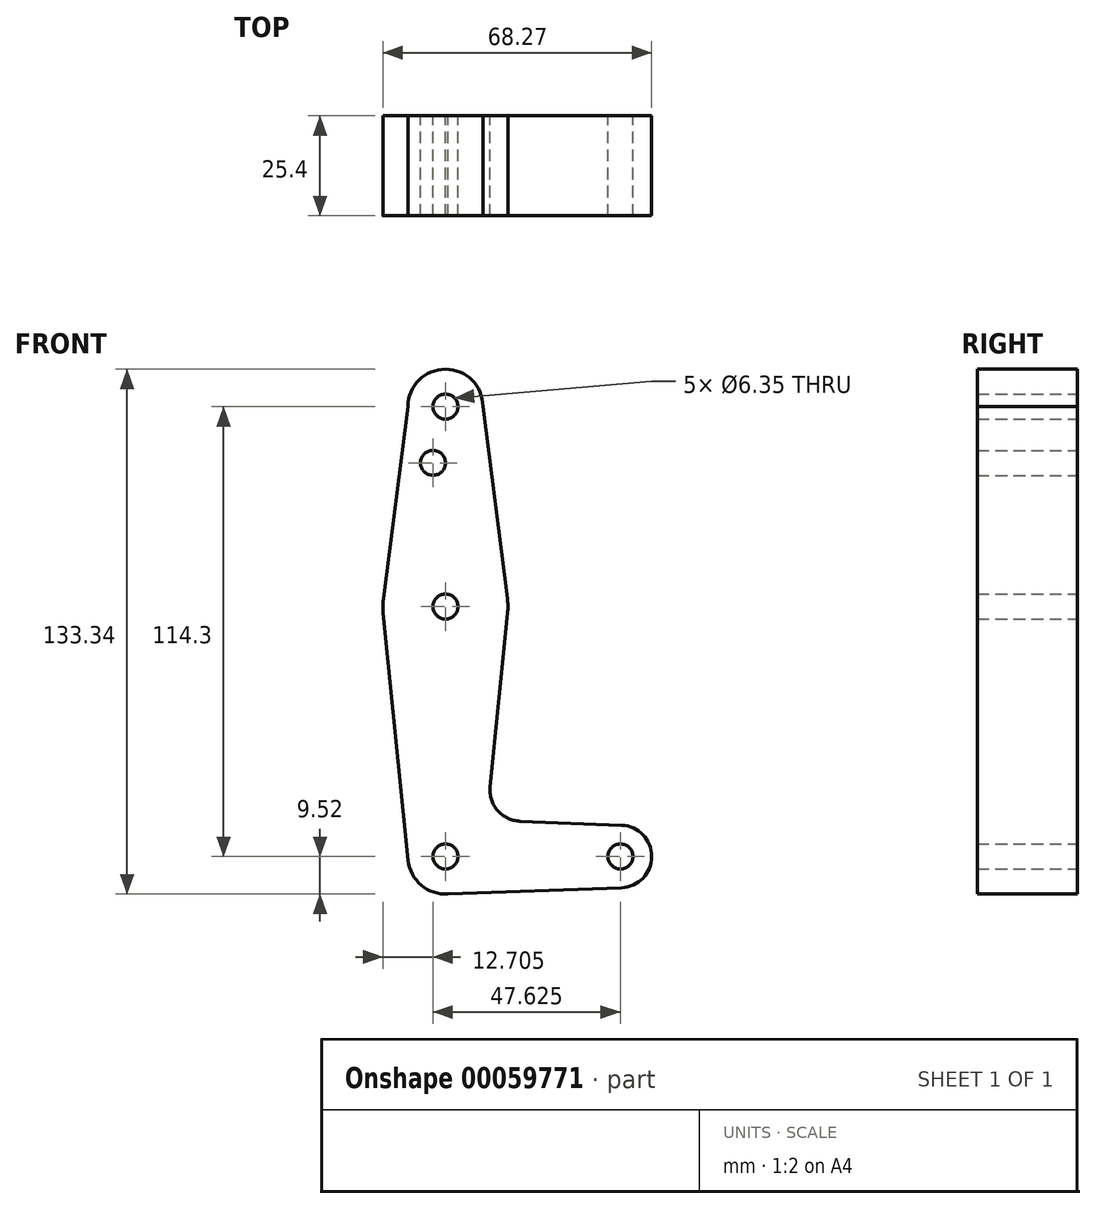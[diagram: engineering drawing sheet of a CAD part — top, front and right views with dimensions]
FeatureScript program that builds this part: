
annotation { "Feature Type Name" : "Feature", "Feature Type Description" : "" }
export const myFeature = defineFeature(function(context is Context, id is Id, definition is map)
    precondition{}
    {
        {
            var Q0;
            Q0=qCreatedBy(makeId("Front.planeOp"),FACE);
            var sketch = newSketch(context, id + "F0", { "sketchPlane" : qUnion([Q0])});
            skLineSegment(sketch, "E0", {"start": v(0, 0) * mm, "end": v(0, -114.3) * mm, "construction": true});
            skLineSegment(sketch, "E1", {"start": v(0, -114.3) * mm, "end": v(44.45, -114.3) * mm, "construction": true});
            skCircle(sketch, "E2", {"center": v(0, 0) * mm, "radius": 9.53 * mm});
            skCircle(sketch, "E3", {"center": v(0, -50.8) * mm, "radius": 15.88 * mm});
            skCircle(sketch, "E4", {"center": v(0, -114.3) * mm, "radius": 9.53 * mm});
            skCircle(sketch, "E5", {"center": v(44.45, -114.3) * mm, "radius": 7.94 * mm});
            skLineSegment(sketch, "E6", {"start": v(-9.53, 0) * mm, "end": v(-15.75, -48.8) * mm});
            skLineSegment(sketch, "E7", {"start": v(9.53, 0) * mm, "end": v(15.75, -48.8) * mm});
            skLineSegment(sketch, "E8", {"start": v(-15.8, -52.39) * mm, "end": v(-9.48, -115.25) * mm});
            skLineSegment(sketch, "E9", {"start": v(15.8, -52.39) * mm, "end": v(11.35, -96.58) * mm});
            skLineSegment(sketch, "E10", {"start": v(18.94, -105.32) * mm, "end": v(44.77, -106.37) * mm});
            skLineSegment(sketch, "E11", {"start": v(0, -123.83) * mm, "end": v(44.73, -122.23) * mm});
            skArc(sketch, "E12.filletArc", {"start": v(11.35, -96.58) * mm, "mid": v(13.26, -102.6) * mm, "end": v(18.94, -105.32) * mm});
            skCircle(sketch, "E13", {"center": v(0, 0) * mm, "radius": 3.18 * mm});
            skCircle(sketch, "E14", {"center": v(0, -50.8) * mm, "radius": 3.18 * mm});
            skCircle(sketch, "E15", {"center": v(0, -114.3) * mm, "radius": 3.18 * mm});
            skCircle(sketch, "E16", {"center": v(44.45, -114.3) * mm, "radius": 3.18 * mm});
            skCircle(sketch, "E17", {"center": v(-3.18, -14.27) * mm, "radius": 3.18 * mm});
            skSolve(sketch);
        }
        {
            var Q0;
            Q0 = qSketchRegion(id + "F0", true);
            extrude(context, id + "F1", {"entities" : qUnion([Q0]), "depth" : 25.4 * mm});
        }
    });
